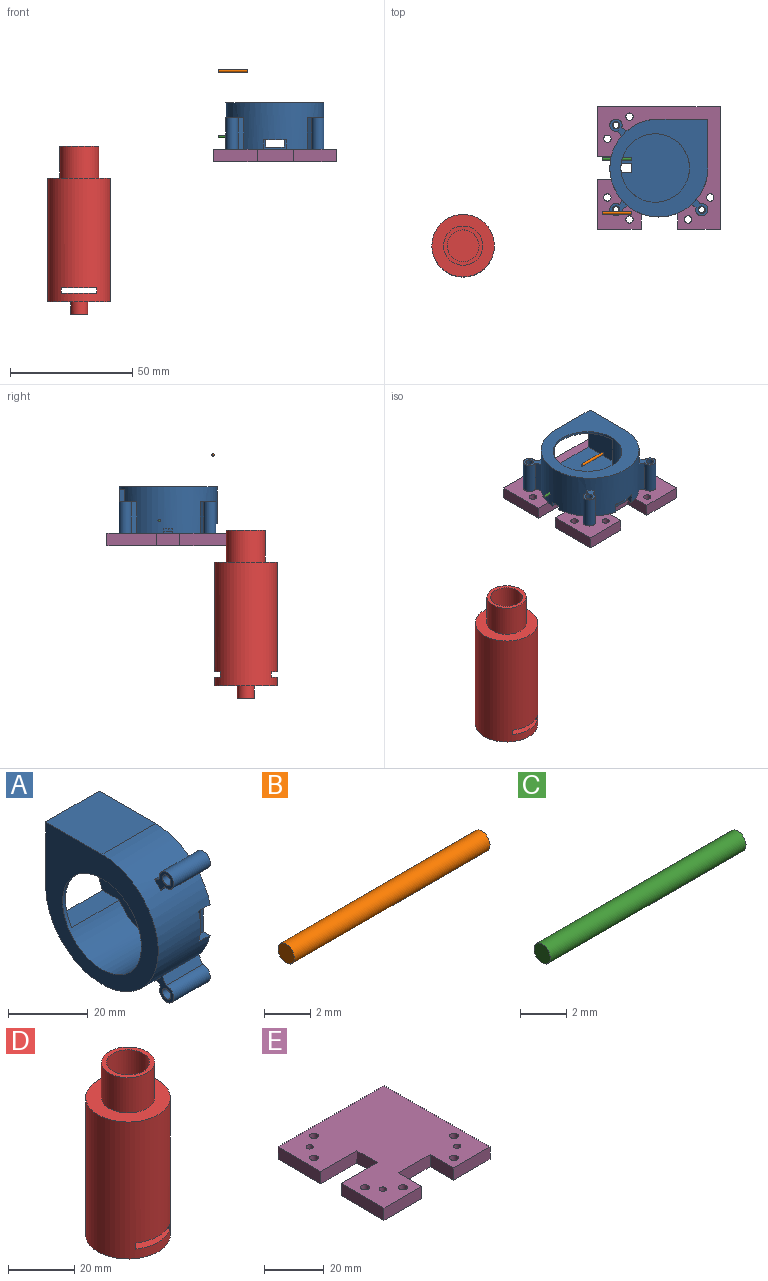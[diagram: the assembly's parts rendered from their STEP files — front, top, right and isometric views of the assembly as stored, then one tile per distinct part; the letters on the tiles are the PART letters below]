
ASSEMBLY  parts=5 mates=3
PART A: 36 faces, bbox 19x40x40 mm
  f0: plane 40x40mm, normal (-1,0,0), area 726.7mm2, adj f3,f5,f8,f33
  f1: plane 9.5x7.02mm, normal (1,0,0), area 51.1mm2, adj f4,f6,f7,f8,f33,f34,f35
  f2: plane 40x39.5mm, normal (1,0,0), area 1339.2mm2, adj f3,f4,f5,f6,f7,f8,f9,f10
  f3: plane 20x19mm, normal (0,0,1), area 380mm2, adj f0,f2,f5,f8
  f4: plane 4x2.43mm, normal (0,0,-1), area 9.7mm2, adj f1,f2,f7,f8
  f5: plane 20x19mm, normal (0,1,0), area 57mm2, adj f0,f2,f3,f8,f28,f29,f31
  f6: plane 4x2.43mm, normal (0,0,1), area 9.7mm2, adj f1,f2,f7,f8
  f7: plane 9.5x4mm, normal (0,-1,0), area 15.5mm2, adj f1,f2,f4,f6,f29,f34,f35
  f8: cylinder r=20mm len=40mm, axis (1,0,0), area 1460.7mm2, adj f0,f1,f2,f3,f4,f5,f6,f10
  f9: plane 3.5x1mm, normal (0,0,-1), area 3.5mm2, adj f2,f10,f11,f29
  f10: plane 8.92x2mm, normal (0,1,0), area 13.5mm2, adj f2,f8,f9,f12,f29,f33
  f11: plane 8.92x2mm, normal (0,-1,0), area 13.5mm2, adj f2,f8,f9,f12,f29,f33
  f12: plane 4.61x3.5mm, normal (1,0,0), area 15.8mm2, adj f8,f10,f11,f33
  f13: cylinder r=1.5mm len=13mm, axis (1,0,0), area 122.5mm2, adj f2,f15
  f14: cylinder r=2.5mm len=13mm, axis (1,0,0), area 175.7mm2, adj f2,f15,f16,f17
  f15: plane 6.89x6.7mm, normal (-1,0,0), area 18mm2, adj f8,f13,f14,f16,f17
  f16: plane 13x1.89mm, normal (0,-0.86,-0.51), area 28.5mm2, adj f2,f8,f14,f15
  f17: plane 13x2.01mm, normal (0,0.52,0.85), area 30.6mm2, adj f2,f8,f14,f15
  f18: cylinder r=1.5mm len=13mm, axis (1,0,0), area 122.5mm2, adj f2,f20
  f19: cylinder r=2.5mm len=13mm, axis (1,0,0), area 175.3mm2, adj f2,f20,f21,f22
  f20: plane 7.26x6.33mm, normal (-1,0,0), area 18.1mm2, adj f8,f18,f19,f21,f22
  f21: plane 13x2.27mm, normal (0,-0.86,0.51), area 34.3mm2, adj f2,f8,f19,f20
  f22: plane 13x1.75mm, normal (0,0.52,-0.86), area 26.6mm2, adj f2,f8,f19,f20
  f23: cylinder r=1.5mm len=13mm, axis (1,0,0), area 122.5mm2, adj f2,f25
  f24: cylinder r=2.5mm len=13mm, axis (1,0,0), area 177.9mm2, adj f2,f25,f26,f27
  f25: plane 7.12x6.97mm, normal (-1,0,0), area 18.7mm2, adj f8,f23,f24,f26,f27
  f26: plane 13x2.28mm, normal (0,-0.5,-0.86), area 34.3mm2, adj f2,f8,f24,f25
  f27: plane 13x2.17mm, normal (0,0.85,0.52), area 33.2mm2, adj f2,f8,f24,f25
  f28: plane 20.21x17mm, normal (0,0,-1), area 343.5mm2, adj f5,f29,f31,f32
  f29: plane 37x34.39mm, normal (-1,0,0), area 925.9mm2, adj f5,f7,f8,f9,f10,f11,f28,f30
  f30: plane 17x6.04mm, normal (0,0,1), area 102.7mm2, adj f8,f29,f31,f33
  f31: plane 28x20.21mm, normal (1,0,0), area 301.4mm2, adj f5,f8,f28,f30,f32,f33
  f32: plane 17x6.5mm, normal (0,1,0), area 110.5mm2, adj f28,f29,f31,f33
  f33: cylinder r=14mm len=28mm, axis (-1,0,0), area 1045mm2, adj f0,f1,f10,f11,f12,f29,f30,f31
  f34: plane 4.02x3mm, normal (0,0,-1), area 12.1mm2, adj f1,f7,f29,f33
  f35: plane 3.18x3mm, normal (0,0,1), area 9.5mm2, adj f1,f7,f29,f33
PART B: 3 faces, bbox 12x1x1 mm
  f0: cylinder r=0.5mm len=12mm, axis (-1,0,0), area 37.7mm2, adj f1,f2
  f1: plane 1x1mm, normal (1,0,0), area 0.8mm2, adj f0
  f2: plane 1x1mm, normal (-1,0,0), area 0.8mm2, adj f0
PART C: 3 faces, bbox 12x1x1 mm
  f0: cylinder r=0.5mm len=12mm, axis (-1,0,0), area 37.7mm2, adj f1,f2
  f1: plane 1x1mm, normal (1,0,0), area 0.8mm2, adj f0
  f2: plane 1x1mm, normal (-1,0,0), area 0.8mm2, adj f0
PART D: 12 faces, bbox 25.5x25.5x68.6 mm
  f0: cylinder r=12.75mm len=50.5mm, axis (0,0,-1), area 3976.2mm2, adj f1,f2,f8,f9,f10,f11
  f1: plane 25.5x25.5mm, normal (0,0,1), area 309.6mm2, adj f0,f3
  f2: plane 25.5x25.5mm, normal (0,0,-1), area 473.3mm2, adj f0,f6
  f3: cylinder r=8mm len=16mm, axis (0,0,-1), area 653.5mm2, adj f1,f4
  f4: plane 16x16mm, normal (0,0,1), area 68.3mm2, adj f3,f5
  f5: cylinder r=6.5mm len=57.75mm, axis (0,0,1), area 2358.6mm2, adj f4,f9
  f6: cylinder r=3.45mm len=6.9mm, axis (0,0,1), area 110.6mm2, adj f2,f7
  f7: plane 6.9x6.9mm, normal (0,0,-1), area 37.4mm2, adj f6
  f8: plane 20.98x2.25mm, normal (1,0,0), area 47.2mm2, adj f0,f9,f11
  f9: plane 25.5x14.5mm, normal (0,0,-1), area 216mm2, adj f0,f5,f8,f10
  f10: plane 20.98x2.25mm, normal (-1,0,0), area 47.2mm2, adj f0,f9,f11
  f11: plane 25.5x14.5mm, normal (0,0,1), area 348.7mm2, adj f0,f8,f10
PART E: 23 faces, bbox 50x50x5 mm
  f0: plane 20.25x5mm, normal (-1,0,0), area 101.2mm2, adj f3,f6,f7,f20
  f1: plane 17.75x5mm, normal (0,-1,0), area 88.8mm2, adj f4,f6,f7,f17
  f2: plane 50x5mm, normal (1,0,0), area 250mm2, adj f3,f5,f6,f7
  f3: plane 50x5mm, normal (0,1,0), area 250mm2, adj f0,f2,f6,f7
  f4: plane 20.25x5mm, normal (-1,0,0), area 101.2mm2, adj f1,f6,f7,f22
  f5: plane 17.25x5mm, normal (0,-1,0), area 86.3mm2, adj f2,f6,f7,f19
  f6: plane 50x50mm, normal (0,0,1), area 2116.8mm2, adj f0,f1,f2,f3,f4,f5,f8,f9
  f7: plane 50x50mm, normal (0,0,-1), area 2116.8mm2, adj f0,f1,f2,f3,f4,f5,f8,f9
  f8: cylinder r=1.23mm len=5mm, axis (0,0,1), area 38.7mm2, adj f6,f7
  f9: cylinder r=1.23mm len=5mm, axis (0,0,1), area 38.7mm2, adj f6,f7
  f10: cylinder r=1.23mm len=5mm, axis (0,0,1), area 38.7mm2, adj f6,f7
  f11: cylinder r=1.5mm len=5mm, axis (0,0,1), area 47.1mm2, adj f6,f7
  f12: cylinder r=1.5mm len=5mm, axis (0,0,1), area 47.1mm2, adj f6,f7
  f13: cylinder r=1.5mm len=5mm, axis (0,0,1), area 47.1mm2, adj f6,f7
  f14: cylinder r=1.5mm len=5mm, axis (0,0,1), area 47.1mm2, adj f6,f7
  f15: cylinder r=1.5mm len=5mm, axis (0,0,1), area 47.1mm2, adj f6,f7
  f16: cylinder r=1.5mm len=5mm, axis (0,0,1), area 47.1mm2, adj f6,f7
  f17: plane 11x5mm, normal (1,0,0), area 55mm2, adj f1,f6,f7,f18
  f18: plane 15x5mm, normal (0,-1,0), area 75mm2, adj f6,f7,f17,f19
  f19: plane 11x5mm, normal (-1,0,0), area 55mm2, adj f5,f6,f7,f18
  f20: plane 17x5mm, normal (0,-1,0), area 85mm2, adj f0,f6,f7,f21
  f21: plane 9.5x5mm, normal (-1,0,0), area 47.5mm2, adj f6,f7,f20,f22
  f22: plane 17x5mm, normal (0,1,0), area 85mm2, adj f4,f6,f7,f21
PLACE A rot(axis=(0,1,0),90deg) t=(76.76,26.92,0.09)mm
PLACE B rot(axis=(0,0.71,0.71),180deg) t=(65.76,-0.21,96.28)mm
PLACE C rot(axis=(0,0.71,0.71),180deg) t=(65.76,20.24,69.46)mm
PLACE D t=(-3.16,-4.76,-101.13)mm
PLACE E t=(76.76,26.92,-43.91)mm
MATE planar B.f0 <-> A.f9  axis (1,0,0) through (65.76,8.57,-6.84)mm
MATE fastened A.f23 <-> E.f10  axis (0,0,-1) through (59.26,44.42,-38.91)mm
MATE planar C.f0 <-> A.f9  axis (1,0,0) through (65.76,30.62,-33.65)mm
